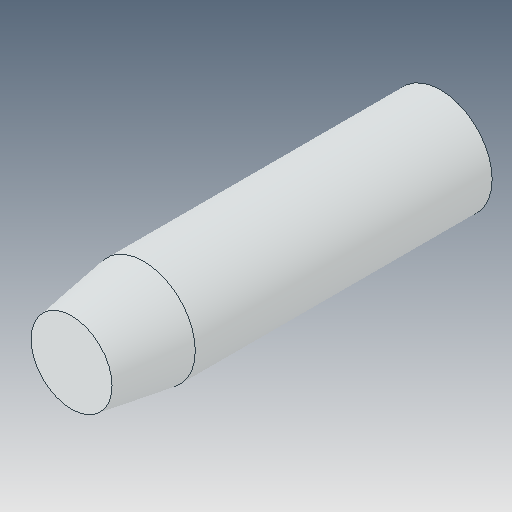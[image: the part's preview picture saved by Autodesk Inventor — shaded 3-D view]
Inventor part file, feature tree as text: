
AUTODESK INVENTOR PART (.ipt)
format: ipt  version: 2023.5 (Build 275446000, 446)  size: 97,280 bytes
history: native  units: in
note: dims shown in document units (in); Inventor stores cm internally (conversion verified against a paired STEP export)
features: chamfer x1
ambient origin geometry x8: Origin, YZ Plane, XZ Plane, XY Plane, X Axis, Y Axis, Z Axis, Center Point
bodies: Solid1 (feature_tree)
feature tree (1):
  chamfer  "Chamfer1"  [1 undecoded]
note: 1 required parameter value undecoded (feature->parameter linkage not recoverable at this tier; creation-order binding heuristic only, values carry confidence <= 0.55)
